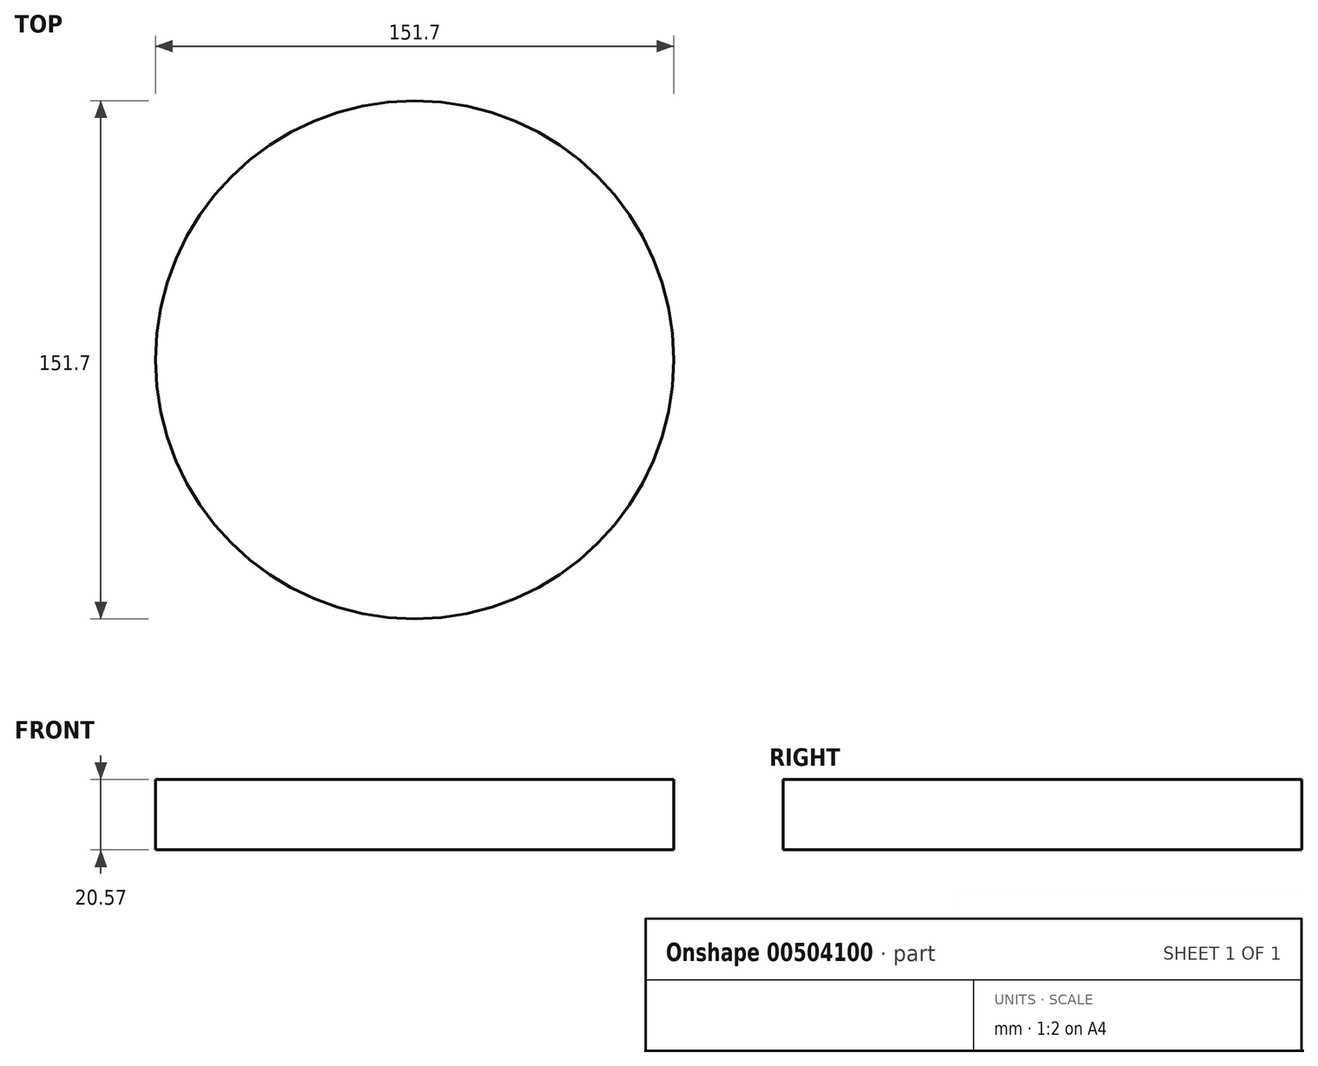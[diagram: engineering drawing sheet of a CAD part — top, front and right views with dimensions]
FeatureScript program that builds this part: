
annotation { "Feature Type Name" : "Feature", "Feature Type Description" : "" }
export const myFeature = defineFeature(function(context is Context, id is Id, definition is map)
    precondition{}
    {
        {
            var Q0;
            Q0=qCreatedBy(makeId("Top.planeOp"),FACE);
            var sketch = newSketch(context, id + "F0", { "sketchPlane" : qUnion([Q0])});
            skCircle(sketch, "E0", {"center": v(0, 0) * mm, "radius": 76.25 * mm});
            skSolve(sketch);
        }
        {
            var Q0;
            Q0=makeQuery(id+"F0.imprint","IMPRINT",FACE,{"disambiguationData":[TD([[makeQuery(id+"F0.imprint","IMPRINT",EDGE,{"derivedFrom":sQuery(id+"F0.wireOp",EDGE,"E0")}),1.0]])]});
            var sketch = newSketch(context, id + "F1", { "sketchPlane" : qUnion([Q0])});
            skCircle(sketch, "E1", {"center": v(0, 0) * mm, "radius": 59.44 * mm});
            skSolve(sketch);
        }
        {
            var Q0;
            Q0=sQuery(id+"F1.wireOp",EDGE,"E1");
            var Q1;
            Q1=sQuery(id+"F0.wireOp",EDGE,"E0");
            extrude(context, id + "F2", {"bodyType" : ToolBodyType.SURFACE, "surfaceEntities" : qUnion([Q0, Q1]), "depth" : 72.03 * mm});
        }
        {
            var Q0;
            Q0=qCreatedBy(makeId("Top.planeOp"),FACE);
            var sketch = newSketch(context, id + "F3", { "sketchPlane" : qUnion([Q0])});
            skCircle(sketch, "E2", {"center": v(0, 0) * mm, "radius": 75.85 * mm});
            skSolve(sketch);
        }
        {
            var Q0;
            Q0 = qSketchRegion(id + "F3", true);
            extrude(context, id + "F4", {"entities" : qUnion([Q0]), "oppositeDirection" : true, "depth" : 20.57 * mm});
        }
    });
